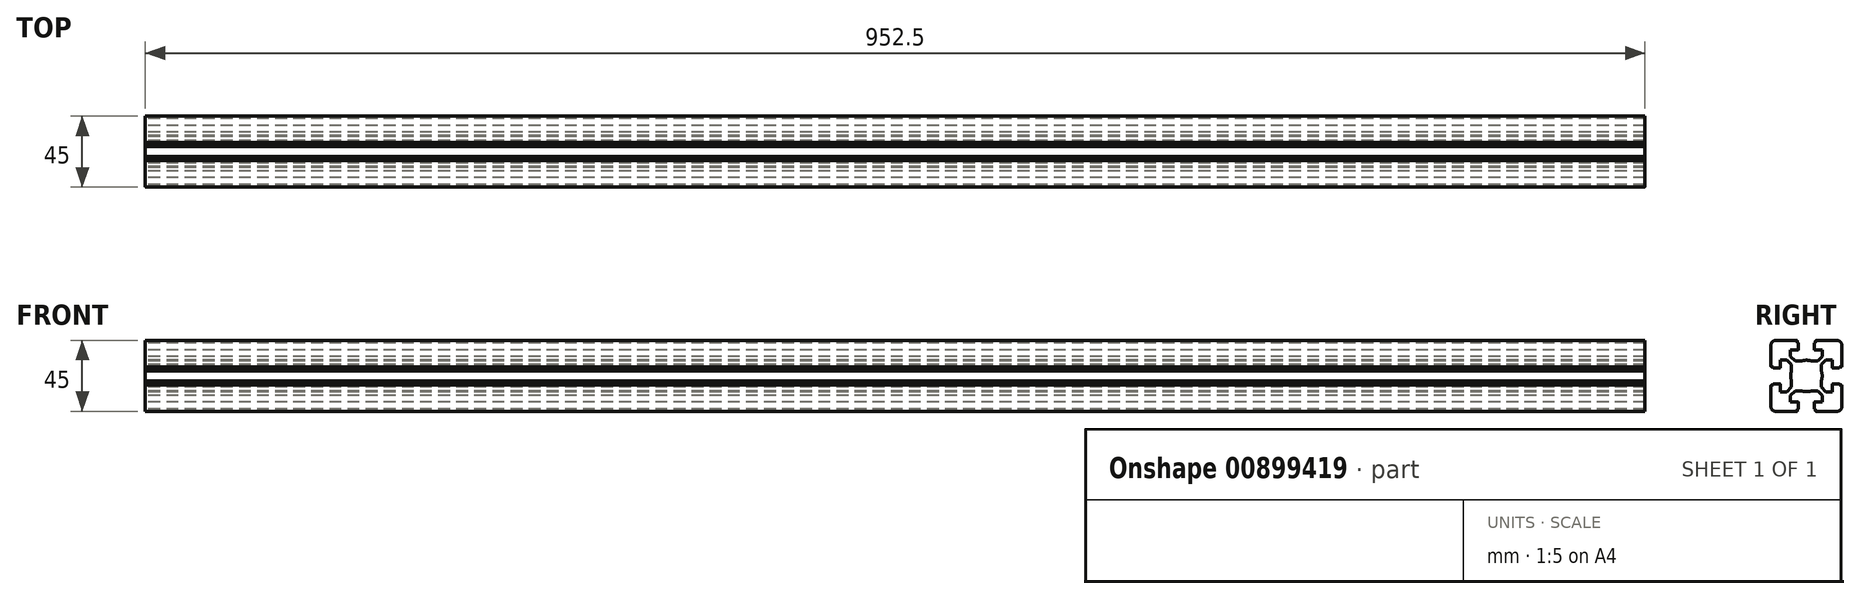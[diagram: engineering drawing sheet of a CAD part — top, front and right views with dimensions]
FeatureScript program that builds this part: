
annotation { "Feature Type Name" : "Feature", "Feature Type Description" : "" }
export const myFeature = defineFeature(function(context is Context, id is Id, definition is map)
    precondition{}
    {
        {
            var Q0;
            Q0=qCreatedBy(makeId("Right.planeOp"),FACE);
            var sketch = newSketch(context, id + "F0", { "sketchPlane" : qUnion([Q0])});
            skLineSegment(sketch, "E0", {"start": v(-20.09, -10.29) * mm, "end": v(-21.29, -10.29) * mm});
            skArc(sketch, "E1", {"start": v(-21.29, -10.29) * mm, "mid": v(-21.5, -10.38) * mm, "end": v(-21.59, -10.59) * mm});
            skLineSegment(sketch, "E2", {"start": v(-21.59, -10.59) * mm, "end": v(-21.59, -23.99) * mm});
            skArc(sketch, "E3", {"start": v(-21.59, -23.99) * mm, "mid": v(-20.7, -26.11) * mm, "end": v(-18.59, -26.99) * mm});
            skLineSegment(sketch, "E4", {"start": v(-18.59, -26.99) * mm, "end": v(-5.19, -26.99) * mm});
            skArc(sketch, "E5", {"start": v(-5.19, -26.99) * mm, "mid": v(-4.98, -26.9) * mm, "end": v(-4.89, -26.69) * mm});
            skLineSegment(sketch, "E6", {"start": v(-4.89, -26.69) * mm, "end": v(-4.89, -25.49) * mm});
            skLineSegment(sketch, "E7", {"start": v(-4.89, -25.49) * mm, "end": v(-4.39, -25.49) * mm});
            skArc(sketch, "E8", {"start": v(-4.39, -25.49) * mm, "mid": v(-4.18, -25.4) * mm, "end": v(-4.09, -25.19) * mm});
            skLineSegment(sketch, "E9", {"start": v(-4.09, -25.19) * mm, "end": v(-4.09, -21.29) * mm});
            skArc(sketch, "E10", {"start": v(-4.09, -21.29) * mm, "mid": v(-4.18, -21.08) * mm, "end": v(-4.39, -20.99) * mm});
            skLineSegment(sketch, "E11", {"start": v(-4.39, -20.99) * mm, "end": v(-9.14, -20.99) * mm});
            skLineSegment(sketch, "E12", {"start": v(-9.14, -20.99) * mm, "end": v(-9.14, -16.88) * mm});
            skLineSegment(sketch, "E13", {"start": v(-9.14, -16.88) * mm, "end": v(-6.25, -13.99) * mm});
            skLineSegment(sketch, "E14", {"start": v(-6.25, -13.99) * mm, "end": v(-2.21, -13.99) * mm});
            skArc(sketch, "E15", {"start": v(-2.21, -13.99) * mm, "mid": v(0.91, -14.49) * mm, "end": v(4.03, -13.99) * mm});
            skLineSegment(sketch, "E16", {"start": v(-20.09, -10.29) * mm, "end": v(-20.09, -9.79) * mm});
            skArc(sketch, "E17", {"start": v(-20.09, -9.79) * mm, "mid": v(-20, -9.58) * mm, "end": v(-19.79, -9.49) * mm});
            skLineSegment(sketch, "E18", {"start": v(-19.79, -9.49) * mm, "end": v(-15.89, -9.49) * mm});
            skArc(sketch, "E19", {"start": v(-15.89, -9.49) * mm, "mid": v(-15.68, -9.58) * mm, "end": v(-15.59, -9.79) * mm});
            skLineSegment(sketch, "E20", {"start": v(-15.59, -9.79) * mm, "end": v(-15.59, -14.54) * mm});
            skLineSegment(sketch, "E21", {"start": v(-15.59, -14.54) * mm, "end": v(-11.48, -14.54) * mm});
            skLineSegment(sketch, "E22", {"start": v(-11.48, -14.54) * mm, "end": v(-8.59, -11.65) * mm});
            skLineSegment(sketch, "E23", {"start": v(-8.59, -11.65) * mm, "end": v(-8.59, -7.61) * mm});
            skLineSegment(sketch, "E24", {"start": v(29.82, -4.49) * mm, "end": v(-31.05, -4.49) * mm});
            skLineSegment(sketch, "E25.MirrorCS", {"start": v(6.71, -25.49) * mm, "end": v(6.21, -25.49) * mm});
            skArc(sketch, "E26.MirrorCS", {"start": v(7.01, -26.99) * mm, "mid": v(6.8, -26.9) * mm, "end": v(6.71, -26.69) * mm});
            skLineSegment(sketch, "E27.MirrorCS", {"start": v(10.41, -11.65) * mm, "end": v(10.41, -7.61) * mm});
            skArc(sketch, "E28.MirrorCS", {"start": v(6.21, -25.49) * mm, "mid": v(6, -25.4) * mm, "end": v(5.91, -25.19) * mm});
            skLineSegment(sketch, "E29.MirrorCS", {"start": v(6.71, -26.69) * mm, "end": v(6.71, -25.49) * mm});
            skArc(sketch, "E30.MirrorCS", {"start": v(5.91, -21.29) * mm, "mid": v(6, -21.08) * mm, "end": v(6.21, -20.99) * mm});
            skLineSegment(sketch, "E31.MirrorCS", {"start": v(10.96, -16.88) * mm, "end": v(8.07, -13.99) * mm});
            skLineSegment(sketch, "E32.MirrorCS", {"start": v(13.3, -14.54) * mm, "end": v(10.41, -11.65) * mm});
            skLineSegment(sketch, "E33.MirrorCS", {"start": v(17.41, -14.54) * mm, "end": v(13.3, -14.54) * mm});
            skLineSegment(sketch, "E34.MirrorCS", {"start": v(17.41, -9.79) * mm, "end": v(17.41, -14.54) * mm});
            skLineSegment(sketch, "E35.MirrorCS", {"start": v(6.21, -20.99) * mm, "end": v(10.96, -20.99) * mm});
            skLineSegment(sketch, "E36.MirrorCS", {"start": v(8.07, -13.99) * mm, "end": v(4.03, -13.99) * mm});
            skArc(sketch, "E37.MirrorCS", {"start": v(4.03, -13.99) * mm, "mid": v(0.91, -14.49) * mm, "end": v(-2.21, -13.99) * mm});
            skLineSegment(sketch, "E38.MirrorCS", {"start": v(10.96, -20.99) * mm, "end": v(10.96, -16.88) * mm});
            skLineSegment(sketch, "E39.MirrorCS", {"start": v(5.91, -25.19) * mm, "end": v(5.91, -21.29) * mm});
            skArc(sketch, "E40.MirrorCS", {"start": v(23.41, -23.99) * mm, "mid": v(22.53, -26.11) * mm, "end": v(20.41, -26.99) * mm});
            skLineSegment(sketch, "E41.MirrorCS", {"start": v(20.41, -26.99) * mm, "end": v(7.01, -26.99) * mm});
            skLineSegment(sketch, "E42.MirrorCS", {"start": v(23.41, -10.59) * mm, "end": v(23.41, -23.99) * mm});
            skArc(sketch, "E43.MirrorCS", {"start": v(17.71, -9.49) * mm, "mid": v(17.5, -9.58) * mm, "end": v(17.41, -9.79) * mm});
            skArc(sketch, "E44.MirrorCS", {"start": v(23.11, -10.29) * mm, "mid": v(23.32, -10.38) * mm, "end": v(23.41, -10.59) * mm});
            skLineSegment(sketch, "E45.MirrorCS", {"start": v(21.91, -10.29) * mm, "end": v(21.91, -9.79) * mm});
            skLineSegment(sketch, "E46.MirrorCS", {"start": v(21.91, -10.29) * mm, "end": v(23.11, -10.29) * mm});
            skArc(sketch, "E47.MirrorCS", {"start": v(21.91, -9.79) * mm, "mid": v(21.82, -9.58) * mm, "end": v(21.61, -9.49) * mm});
            skLineSegment(sketch, "E48.MirrorCS", {"start": v(21.61, -9.49) * mm, "end": v(17.71, -9.49) * mm});
            skLineSegment(sketch, "E49.MirrorCS", {"start": v(6.71, 16.51) * mm, "end": v(6.21, 16.51) * mm});
            skArc(sketch, "E50.MirrorCS", {"start": v(-4.39, 16.51) * mm, "mid": v(-4.18, 16.42) * mm, "end": v(-4.09, 16.21) * mm});
            skLineSegment(sketch, "E51.MirrorCS", {"start": v(-4.89, 16.51) * mm, "end": v(-4.39, 16.51) * mm});
            skArc(sketch, "E52.MirrorCS", {"start": v(5.91, 12.31) * mm, "mid": v(6, 12.1) * mm, "end": v(6.21, 12.01) * mm});
            skLineSegment(sketch, "E53.MirrorCS", {"start": v(6.71, 17.71) * mm, "end": v(6.71, 16.51) * mm});
            skLineSegment(sketch, "E54.MirrorCS", {"start": v(-4.89, 17.71) * mm, "end": v(-4.89, 16.51) * mm});
            skArc(sketch, "E55.MirrorCS", {"start": v(-5.19, 18.01) * mm, "mid": v(-4.98, 17.92) * mm, "end": v(-4.89, 17.71) * mm});
            skArc(sketch, "E56.MirrorCS", {"start": v(-4.09, 12.31) * mm, "mid": v(-4.18, 12.1) * mm, "end": v(-4.39, 12.01) * mm});
            skArc(sketch, "E57.MirrorCS", {"start": v(7.01, 18.01) * mm, "mid": v(6.8, 17.92) * mm, "end": v(6.71, 17.71) * mm});
            skArc(sketch, "E58.MirrorCS", {"start": v(6.21, 16.51) * mm, "mid": v(6, 16.42) * mm, "end": v(5.91, 16.21) * mm});
            skArc(sketch, "E59.MirrorCS", {"start": v(23.11, 1.31) * mm, "mid": v(23.32, 1.4) * mm, "end": v(23.41, 1.61) * mm});
            skLineSegment(sketch, "E60.MirrorCS", {"start": v(21.91, 1.31) * mm, "end": v(21.91, 0.81) * mm});
            skArc(sketch, "E61.MirrorCS", {"start": v(-15.89, 0.51) * mm, "mid": v(-15.68, 0.6) * mm, "end": v(-15.59, 0.81) * mm});
            skArc(sketch, "E62.MirrorCS", {"start": v(-21.29, 1.31) * mm, "mid": v(-21.5, 1.4) * mm, "end": v(-21.59, 1.61) * mm});
            skArc(sketch, "E63.MirrorCS", {"start": v(17.71, 0.51) * mm, "mid": v(17.5, 0.6) * mm, "end": v(17.41, 0.81) * mm});
            skArc(sketch, "E64.MirrorCS", {"start": v(21.91, 0.81) * mm, "mid": v(21.82, 0.6) * mm, "end": v(21.61, 0.51) * mm});
            skLineSegment(sketch, "E65.MirrorCS", {"start": v(21.91, 1.31) * mm, "end": v(23.11, 1.31) * mm});
            skArc(sketch, "E66.MirrorCS", {"start": v(14.31, 5.31) * mm, "mid": v(14.1, 5.4) * mm, "end": v(14.01, 5.61) * mm});
            skArc(sketch, "E67.MirrorCS", {"start": v(-20.09, 0.81) * mm, "mid": v(-20, 0.6) * mm, "end": v(-19.79, 0.51) * mm});
            skLineSegment(sketch, "E68.MirrorCS", {"start": v(-20.09, 1.31) * mm, "end": v(-21.29, 1.31) * mm});
            skLineSegment(sketch, "E69.MirrorCS", {"start": v(-20.09, 1.31) * mm, "end": v(-20.09, 0.81) * mm});
            skLineSegment(sketch, "E70.MirrorCS", {"start": v(8.07, 5.01) * mm, "end": v(4.03, 5.01) * mm});
            skLineSegment(sketch, "E71.MirrorCS", {"start": v(-4.09, 16.21) * mm, "end": v(-4.09, 12.31) * mm});
            skLineSegment(sketch, "E72.MirrorCS", {"start": v(-9.14, 12.01) * mm, "end": v(-9.14, 7.9) * mm});
            skLineSegment(sketch, "E73.MirrorCS", {"start": v(-15.59, 5.56) * mm, "end": v(-11.48, 5.56) * mm});
            skLineSegment(sketch, "E74.MirrorCS", {"start": v(-4.39, 12.01) * mm, "end": v(-9.14, 12.01) * mm});
            skLineSegment(sketch, "E75.MirrorCS", {"start": v(-9.14, 7.9) * mm, "end": v(-6.25, 5.01) * mm});
            skLineSegment(sketch, "E76.MirrorCS", {"start": v(10.96, 12.01) * mm, "end": v(10.96, 7.9) * mm});
            skArc(sketch, "E77.MirrorCS", {"start": v(-21.59, 15.01) * mm, "mid": v(-20.7, 17.13) * mm, "end": v(-18.59, 18.01) * mm});
            skLineSegment(sketch, "E78.MirrorCS", {"start": v(23.41, 1.61) * mm, "end": v(23.41, 15.01) * mm});
            skLineSegment(sketch, "E79.MirrorCS", {"start": v(13.3, 5.56) * mm, "end": v(10.41, 2.67) * mm});
            skLineSegment(sketch, "E80.MirrorCS", {"start": v(-8.59, 2.67) * mm, "end": v(-8.59, -1.37) * mm});
            skLineSegment(sketch, "E81.MirrorCS", {"start": v(-15.59, 0.81) * mm, "end": v(-15.59, 5.56) * mm});
            skLineSegment(sketch, "E82.MirrorCS", {"start": v(10.41, 2.67) * mm, "end": v(10.41, -1.37) * mm});
            skLineSegment(sketch, "E83.MirrorCS", {"start": v(-18.59, 18.01) * mm, "end": v(-5.19, 18.01) * mm});
            skLineSegment(sketch, "E84.MirrorCS", {"start": v(10.96, 7.9) * mm, "end": v(8.07, 5.01) * mm});
            skLineSegment(sketch, "E85.MirrorCS", {"start": v(17.41, 5.56) * mm, "end": v(13.3, 5.56) * mm});
            skArc(sketch, "E86.MirrorCS", {"start": v(23.41, 15.01) * mm, "mid": v(22.53, 17.13) * mm, "end": v(20.41, 18.01) * mm});
            skLineSegment(sketch, "E87.MirrorCS", {"start": v(5.91, 16.21) * mm, "end": v(5.91, 12.31) * mm});
            skLineSegment(sketch, "E88.MirrorCS", {"start": v(17.41, 0.81) * mm, "end": v(17.41, 5.56) * mm});
            skLineSegment(sketch, "E89.MirrorCS", {"start": v(-11.48, 5.56) * mm, "end": v(-8.59, 2.67) * mm});
            skLineSegment(sketch, "E90.MirrorCS", {"start": v(-6.25, 5.01) * mm, "end": v(-2.21, 5.01) * mm});
            skLineSegment(sketch, "E91.MirrorCS", {"start": v(-21.59, 1.61) * mm, "end": v(-21.59, 15.01) * mm});
            skArc(sketch, "E92.MirrorCS", {"start": v(4.03, 5.01) * mm, "mid": v(0.91, 5.51) * mm, "end": v(-2.21, 5.01) * mm});
            skLineSegment(sketch, "E93.MirrorCS", {"start": v(6.21, 12.01) * mm, "end": v(10.96, 12.01) * mm});
            skArc(sketch, "E94.MirrorCS", {"start": v(-2.21, 5.01) * mm, "mid": v(0.91, 5.51) * mm, "end": v(4.03, 5.01) * mm});
            skLineSegment(sketch, "E95.MirrorCS", {"start": v(20.41, 18.01) * mm, "end": v(7.01, 18.01) * mm});
            skLineSegment(sketch, "E96.MirrorCS", {"start": v(-19.79, 0.51) * mm, "end": v(-15.89, 0.51) * mm});
            skLineSegment(sketch, "E97.MirrorCS", {"start": v(21.61, 0.51) * mm, "end": v(17.71, 0.51) * mm});
            skLineSegment(sketch, "E98.MirrorCS", {"start": v(0.91, -27.65) * mm, "end": v(0.91, 19.82) * mm});
            skArc(sketch, "E99", {"start": v(-8.59, -1.37) * mm, "mid": v(-9.09, -4.49) * mm, "end": v(-8.59, -7.61) * mm});
            skArc(sketch, "E100", {"start": v(10.41, -7.61) * mm, "mid": v(10.91, -4.49) * mm, "end": v(10.41, -1.37) * mm});
            skSolve(sketch);
        }
        {
            var Q0;
            Q0=qSketchRegion(id+"F0",true);
            extrude(context, id + "F1", {"entities" : qUnion([Q0]), "depth" : 952.5 * mm, "offsetDistance" : 25.4 * mm});
        }
    });
